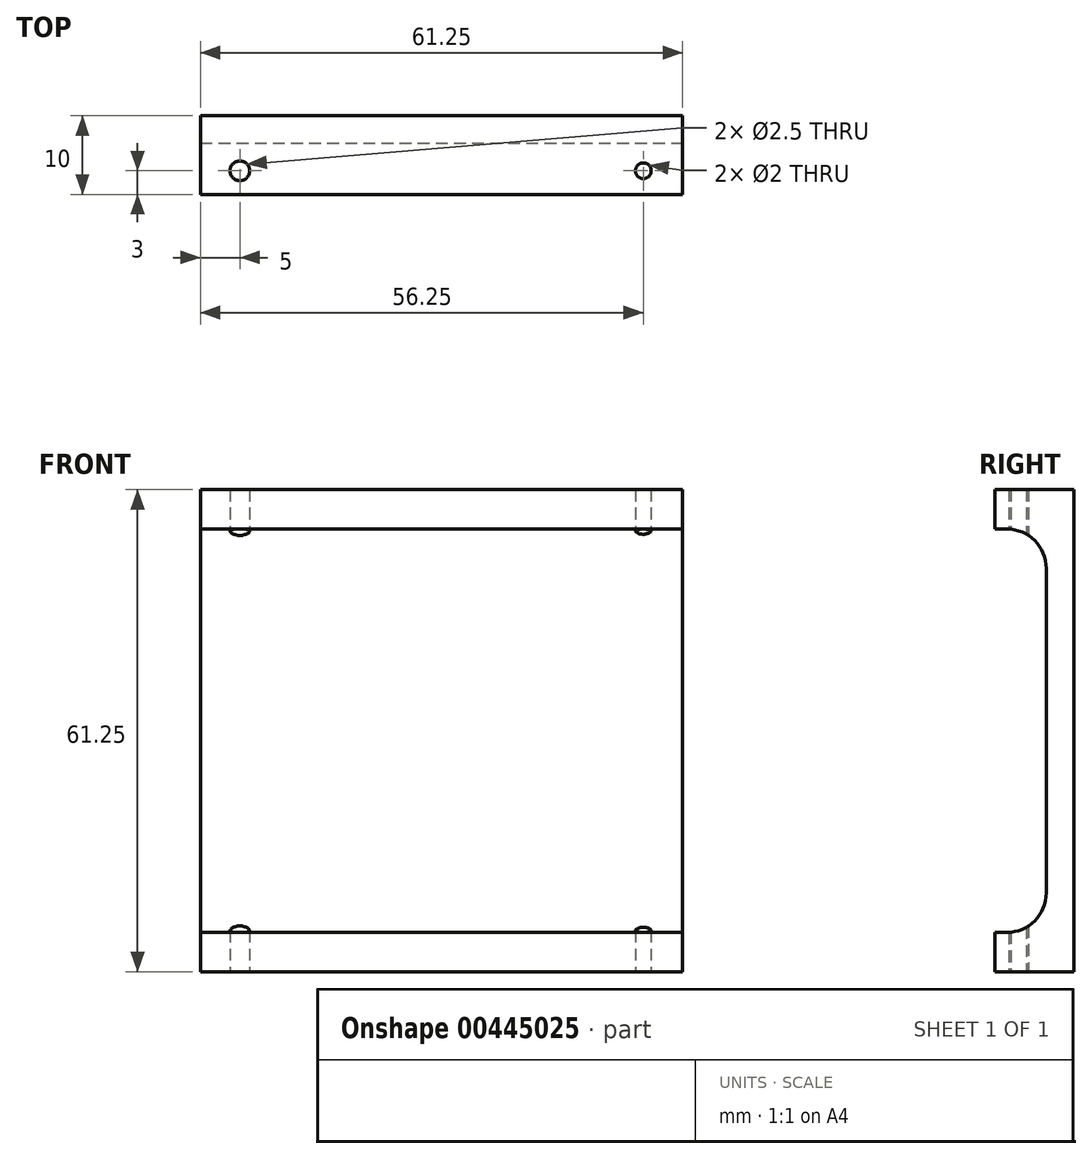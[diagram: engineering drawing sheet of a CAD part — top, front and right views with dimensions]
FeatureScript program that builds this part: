
annotation { "Feature Type Name" : "Feature", "Feature Type Description" : "" }
export const myFeature = defineFeature(function(context is Context, id is Id, definition is map)
    precondition{}
    {
        {
            var Q0;
            Q0=qCreatedBy(makeId("Front.planeOp"),FACE);
            var sketch = newSketch(context, id + "F0", { "sketchPlane" : qUnion([Q0])});
            skLineSegment(sketch, "E0.bottom", {"start": v(0, 0) * mm, "end": v(61.25, 0) * mm});
            skLineSegment(sketch, "E0.top", {"start": v(0, 61.25) * mm, "end": v(61.25, 61.25) * mm});
            skLineSegment(sketch, "E0.left", {"start": v(0, 0) * mm, "end": v(0, 61.25) * mm});
            skLineSegment(sketch, "E0.right", {"start": v(61.25, 0) * mm, "end": v(61.25, 61.25) * mm});
            skSolve(sketch);
        }
        {
            var Q0;
            Q0 = qSketchRegion(id + "F0", true);
            extrude(context, id + "F1", {"entities" : qUnion([Q0]), "depth" : 10 * mm});
        }
        {
            var Q0;
            Q0=makeQuery(id+"F1.opExtrude","SWEPT_FACE",FACE,{"disambiguationData":[OSD([sQuery(id+"F0.wireOp",EDGE,"E0.right")])]});
            var sketch = newSketch(context, id + "F2", { "sketchPlane" : qUnion([Q0])});
            skLineSegment(sketch, "E1", {"start": v(-10, 5) * mm, "end": v(-8.5, 5) * mm});
            skLineSegment(sketch, "E2", {"start": v(-3.5, 10) * mm, "end": v(-3.5, 51.25) * mm});
            skLineSegment(sketch, "E3", {"start": v(-8.5, 56.25) * mm, "end": v(-10, 56.25) * mm});
            skLineSegment(sketch, "E4", {"start": v(-10, 56.25) * mm, "end": v(-10, 5) * mm});
            skPoint(sketch, "E5.visualSharp", {"position": v(-3.5, 5) * mm});
            skArc(sketch, "E5.filletArc", {"start": v(-8.5, 5) * mm, "mid": v(-4.96, 6.46) * mm, "end": v(-3.5, 10) * mm});
            skPoint(sketch, "E6.visualSharp", {"position": v(-3.5, 56.25) * mm});
            skArc(sketch, "E6.filletArc", {"start": v(-3.5, 51.25) * mm, "mid": v(-4.96, 54.79) * mm, "end": v(-8.5, 56.25) * mm});
            skSolve(sketch);
        }
        {
            var Q0;
            Q0=makeQuery(id+"F2.imprint","IMPRINT",FACE,{"disambiguationData":[TD([[makeQuery(id+"F2.imprint","IMPRINT",EDGE,{"derivedFrom":sQuery(id+"F2.wireOp",EDGE,"E1")}),1.0]])]});
            extrude(context, id + "F3", {"entities" : qUnion([Q0]), "operationType" : NewBodyOperationType.REMOVE, "oppositeDirection" : true, "depth" : 80 * mm});
        }
        {
            var Q0;
            Q0=makeQuery(id+"F1.opExtrude","SWEPT_FACE",FACE,{"disambiguationData":[OSD([sQuery(id+"F0.wireOp",EDGE,"E0.bottom")])]});
            var sketch = newSketch(context, id + "F4", { "sketchPlane" : qUnion([Q0])});
            skCircle(sketch, "E7", {"center": v(56.25, 7) * mm, "radius": 1 * mm});
            skCircle(sketch, "E8", {"center": v(5, 7) * mm, "radius": 1.25 * mm});
            skSolve(sketch);
        }
        {
            var Q0;
            Q0 = qSketchRegion(id + "F4", true);
            extrude(context, id + "F5", {"entities" : qUnion([Q0]), "operationType" : NewBodyOperationType.REMOVE, "oppositeDirection" : true, "depth" : 80 * mm});
        }
    });
